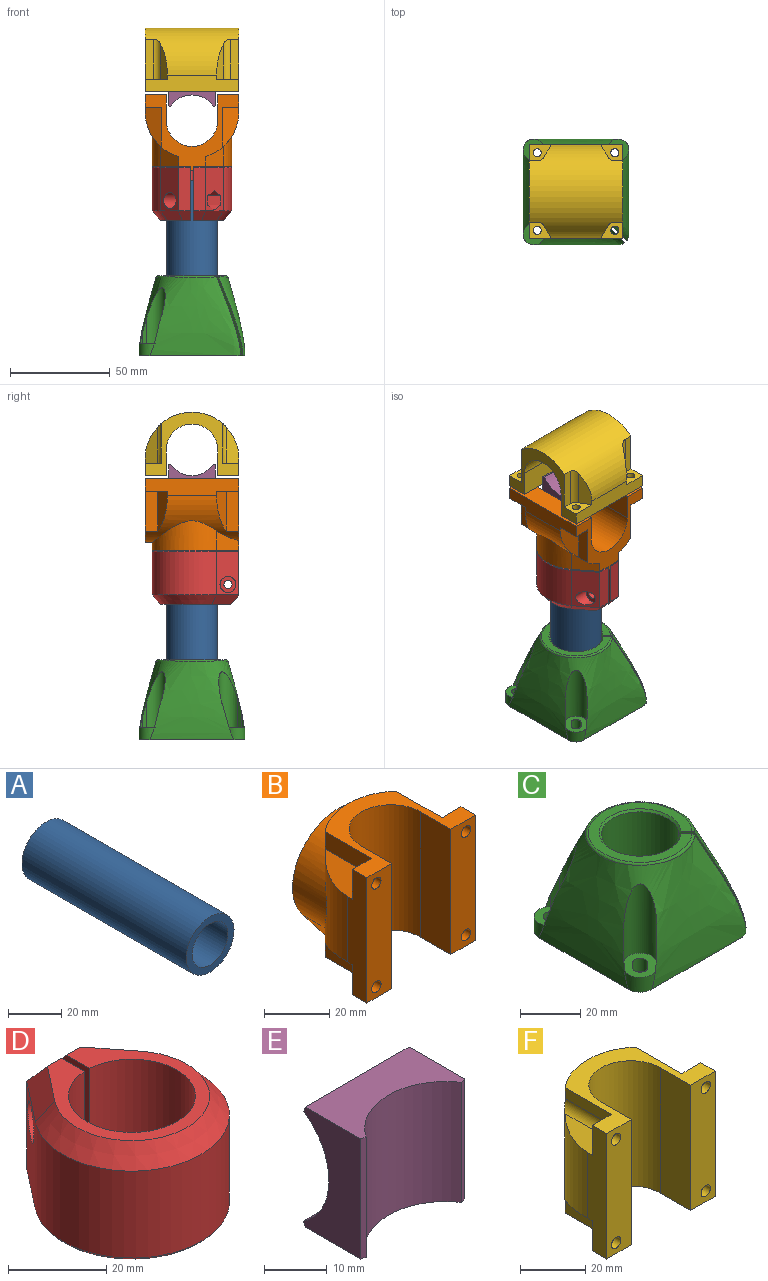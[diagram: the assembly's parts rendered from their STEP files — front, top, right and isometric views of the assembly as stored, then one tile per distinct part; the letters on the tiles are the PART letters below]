
ASSEMBLY  parts=6 mates=5
PART A: 4 faces, bbox 25.4x87x25.4 mm
  f0: cylinder r=9.5mm len=87mm, axis (0,-1,0), area 5193.1mm2, adj f2,f3
  f1: cylinder r=12.7mm len=87mm, axis (0,-1,0), area 6942.3mm2, adj f2,f3
  f2: plane 25.4x25.4mm, normal (0,1,0), area 223.2mm2, adj f0,f1
  f3: plane 25.4x25.4mm, normal (0,-1,0), area 223.2mm2, adj f0,f1
PART B: 35 faces, bbox 47x37.9x47 mm
  f0: plane 47x8.4mm, normal (1,0,0), area 346.6mm2, adj f2,f10,f11,f18,f30,f31,f32,f34
  f1: plane 47x8.4mm, normal (-1,0,0), area 346.6mm2, adj f2,f4,f10,f18,f23,f25,f27,f28
  f2: cylinder r=23.5mm len=47mm, axis (0,0,-1), area 1212.5mm2, adj f0,f1,f5,f6,f7,f10,f18,f23
  f3: cylinder r=12.85mm len=47mm, axis (0,0,-1), area 1889.1mm2, adj f8,f10,f16,f17,f18
  f4: plane 47x10.65mm, normal (0,-1,0), area 474.8mm2, adj f1,f10,f16,f18,f21,f22
  f5: plane 11.3x9.92mm, normal (0.79,0,-0.62), area 100.9mm2, adj f2,f6,f9,f10
  f6: cylinder r=19.8mm len=39.6mm, axis (0,1,0), area 902.1mm2, adj f2,f5,f7,f9
  f7: plane 11.3x9.92mm, normal (-0.79,0,-0.62), area 100.9mm2, adj f2,f6,f9,f10
  f8: cylinder r=2.02mm len=10.16mm, axis (0,1,0), area 128.3mm2, adj f3,f9
  f9: plane 43.3x39.6mm, normal (0,1,0), area 1288.9mm2, adj f5,f6,f7,f8,f10,f12,f13,f14
  f10: plane 47x37.9mm, normal (0,0,-1), area 490.6mm2, adj f0,f1,f2,f3,f4,f5,f7,f9
  f11: plane 47x10.65mm, normal (0,-1,0), area 474.8mm2, adj f0,f10,f17,f18,f19,f20
  f12: plane 10.8x2mm, normal (1,0,0), area 21.6mm2, adj f9,f10,f13,f15
  f13: cylinder r=0.75mm len=2mm, axis (0,-1,0), area 4.7mm2, adj f9,f12,f14,f15
  f14: plane 10.8x2mm, normal (-1,0,0), area 21.6mm2, adj f9,f10,f13,f15
  f15: plane 11.55x1.5mm, normal (0,1,0), area 17.1mm2, adj f10,f12,f13,f14
  f16: plane 47x13mm, normal (1,0,0), area 611mm2, adj f3,f4,f10,f18
  f17: plane 47x13mm, normal (-1,0,0), area 611mm2, adj f3,f10,f11,f18
  f18: plane 47x31.9mm, normal (0,0,1), area 429.2mm2, adj f0,f1,f2,f3,f4,f11,f16,f17
  f19: cylinder r=2.02mm len=6.25mm, axis (0,1,0), area 79.5mm2, adj f11,f34
  f20: cylinder r=2.02mm len=6.25mm, axis (0,1,0), area 79.5mm2, adj f11,f31
  f21: cylinder r=2.02mm len=6.25mm, axis (0,1,0), area 79.5mm2, adj f4,f28
  f22: cylinder r=2.02mm len=6.25mm, axis (0,1,0), area 79.5mm2, adj f4,f25
  f23: plane 19.99x8.2mm, normal (-0.5,0,0.87), area 137.6mm2, adj f1,f2,f24,f25
  f24: plane 19.99x6.47mm, normal (-1,0,0), area 129.3mm2, adj f2,f18,f23,f25
  f25: plane 11.2x8.2mm, normal (0,1,0), area 59.6mm2, adj f1,f18,f22,f23,f24
  f26: plane 19.99x6.47mm, normal (-1,0,0), area 129.3mm2, adj f2,f10,f27,f28
  f27: plane 19.99x8.2mm, normal (-0.5,0,-0.87), area 137.6mm2, adj f1,f2,f26,f28
  f28: plane 11.2x8.2mm, normal (0,1,0), area 59.6mm2, adj f1,f10,f21,f26,f27
  f29: plane 19.99x6.47mm, normal (1,0,0), area 129.3mm2, adj f2,f10,f30,f31
  f30: plane 19.99x8.2mm, normal (0.5,0,-0.87), area 137.6mm2, adj f0,f2,f29,f31
  f31: plane 11.2x8.2mm, normal (0,1,0), area 59.6mm2, adj f0,f10,f20,f29,f30
  f32: plane 19.99x8.2mm, normal (0.5,0,0.87), area 137.6mm2, adj f0,f2,f33,f34
  f33: plane 19.99x6.47mm, normal (1,0,0), area 129.3mm2, adj f2,f18,f32,f34
  f34: plane 11.2x8.2mm, normal (0,1,0), area 59.6mm2, adj f0,f18,f19,f32,f33
PART C: 56 faces, bbox 53.3x53.3x40.3 mm
  f0: bspline ~53x53mm, area 5579.9mm2, adj f13,f16,f17,f18,f19,f20,f21,f22
  f1: plane 5.25x2.12mm, normal (0.71,-0.71,0), area 15.7mm2, adj f2,f4,f35,f49
  f2: cylinder r=2.5mm len=5.25mm, axis (0,0,1), area 41.2mm2, adj f1,f3,f35,f50
  f3: plane 5.25x2.12mm, normal (-0.71,0.71,0), area 15.7mm2, adj f2,f4,f35,f48
  f4: cylinder r=2.5mm len=5.25mm, axis (0,0,1), area 41.2mm2, adj f1,f3,f35,f47
  f5: plane 5.25x2.12mm, normal (-0.71,-0.71,0), area 15.7mm2, adj f6,f8,f29,f45
  f6: cylinder r=2.5mm len=5.25mm, axis (0,0,1), area 41.2mm2, adj f5,f7,f29,f46
  f7: plane 5.25x2.12mm, normal (0.71,0.71,0), area 15.7mm2, adj f6,f8,f29,f44
  f8: cylinder r=2.5mm len=5.25mm, axis (0,0,1), area 41.2mm2, adj f5,f7,f29,f43
  f9: plane 5.25x2.12mm, normal (-0.71,0.71,0), area 15.7mm2, adj f10,f12,f23,f41
  f10: cylinder r=2.5mm len=5.25mm, axis (0,0,1), area 41.2mm2, adj f9,f11,f23,f42
  f11: plane 5.25x2.12mm, normal (0.71,-0.71,0), area 15.7mm2, adj f10,f12,f23,f40
  f12: cylinder r=2.5mm len=5.25mm, axis (0,0,1), area 41.2mm2, adj f9,f11,f23,f39
  f13: plane 53.28x53.28mm, normal (0,0,-1), area 1979.2mm2, adj f0,f36,f37,f38,f39,f40,f41,f42
  f14: plane 34.21x34.2mm, normal (0,0,1), area 340.7mm2, adj f16,f17,f51,f55
  f15: cylinder r=12.85mm len=38.5mm, axis (0,0,1), area 3050.7mm2, adj f16,f17,f51,f53
  f16: plane 39.27x15.79mm, normal (0.71,0.71,0), area 590.7mm2, adj f0,f14,f15,f51,f52,f55
  f17: plane 39.26x15.79mm, normal (-0.71,-0.71,0), area 592.4mm2, adj f0,f14,f15,f51,f54,f55
  f18: cylinder r=5.5mm len=5.12mm, axis (0,0,-1), area 4.7mm2, adj f0,f22,f23
  f19: cylinder r=5.5mm len=7.16mm, axis (0,0,-1), area 7.8mm2, adj f0,f20,f23
  f20: plane 15.57x2.42mm, normal (0.71,-0.71,0), area 34.5mm2, adj f0,f19,f21,f23
  f21: cylinder r=5.5mm len=28.05mm, axis (0,0,-1), area 394.3mm2, adj f0,f20,f22,f23
  f22: plane 12.96x2.34mm, normal (-0.71,0.71,0), area 27.2mm2, adj f0,f18,f21,f23
  f23: plane 13.12x13.12mm, normal (0,0,1), area 93.4mm2, adj f9,f10,f11,f12,f18,f19,f20,f21
  f24: cylinder r=5.5mm len=5.12mm, axis (0,0,-1), area 4.7mm2, adj f0,f28,f29
  f25: cylinder r=5.5mm len=7.16mm, axis (0,0,-1), area 7.8mm2, adj f0,f26,f29
  f26: plane 15.57x2.42mm, normal (0.71,0.71,0), area 34.5mm2, adj f0,f25,f27,f29
  f27: cylinder r=5.5mm len=28.05mm, axis (0,0,-1), area 394.3mm2, adj f0,f26,f28,f29
  f28: plane 12.96x2.34mm, normal (-0.71,-0.71,0), area 27.2mm2, adj f0,f24,f27,f29
  f29: plane 13.12x13.12mm, normal (0,0,1), area 93.4mm2, adj f5,f6,f7,f8,f24,f25,f26,f27
  f30: cylinder r=5.5mm len=5.12mm, axis (0,0,-1), area 4.7mm2, adj f0,f34,f35
  f31: cylinder r=5.5mm len=7.16mm, axis (0,0,-1), area 7.8mm2, adj f0,f32,f35
  f32: plane 15.57x2.42mm, normal (-0.71,0.71,0), area 34.5mm2, adj f0,f31,f33,f35
  f33: cylinder r=5.5mm len=28.05mm, axis (0,0,-1), area 394.3mm2, adj f0,f32,f34,f35
  f34: plane 12.96x2.34mm, normal (0.71,-0.71,0), area 27.2mm2, adj f0,f30,f33,f35
  f35: plane 13.12x13.12mm, normal (0,0,1), area 93.4mm2, adj f1,f2,f3,f4,f30,f31,f32,f33
  f36: cylinder r=5.5mm len=7.91mm, axis (0,0,-1), area 65.9mm2, adj f0,f13,f35
  f37: cylinder r=5.5mm len=7.91mm, axis (0,0,-1), area 65.9mm2, adj f0,f13,f29
  f38: cylinder r=5.5mm len=7.91mm, axis (0,0,-1), area 66mm2, adj f0,f13,f23
  f39: cone r=2.5mm half-angle=45deg, axis (0,0,-1), area 9.6mm2, adj f12,f13,f40,f41
  f40: plane 2.65x2.65mm, normal (0.5,-0.5,-0.71), area 3.2mm2, adj f11,f13,f39,f42
  f41: plane 2.65x2.65mm, normal (-0.5,0.5,-0.71), area 3.2mm2, adj f9,f13,f39,f42
  f42: cone r=2.5mm half-angle=45deg, axis (0,0,-1), area 9.6mm2, adj f10,f13,f40,f41
  f43: cone r=2.5mm half-angle=45deg, axis (0,0,-1), area 9.6mm2, adj f8,f13,f44,f45
  f44: plane 2.65x2.65mm, normal (0.5,0.5,-0.71), area 3.2mm2, adj f7,f13,f43,f46
  f45: plane 2.65x2.65mm, normal (-0.5,-0.5,-0.71), area 3.2mm2, adj f5,f13,f43,f46
  f46: cone r=2.5mm half-angle=45deg, axis (0,0,-1), area 9.6mm2, adj f6,f13,f44,f45
  f47: cone r=2.5mm half-angle=45deg, axis (0,0,-1), area 9.6mm2, adj f4,f13,f48,f49
  f48: plane 2.65x2.65mm, normal (-0.5,0.5,-0.71), area 3.2mm2, adj f3,f13,f47,f50
  f49: plane 2.65x2.65mm, normal (0.5,-0.5,-0.71), area 3.2mm2, adj f1,f13,f47,f50
  f50: cone r=2.5mm half-angle=45deg, axis (0,0,-1), area 9.6mm2, adj f2,f13,f48,f49
  f51: cone r=12.85mm half-angle=45deg, axis (0,0,1), area 86.5mm2, adj f14,f15,f16,f17
  f52: plane 16.22x15.83mm, normal (0.5,0.5,-0.71), area 23.2mm2, adj f0,f13,f16,f53
  f53: cone r=13.6mm half-angle=45deg, axis (0,0,-1), area 85.8mm2, adj f13,f15,f52,f54
  f54: plane 16.22x15.83mm, normal (-0.5,-0.5,-0.71), area 23.2mm2, adj f0,f13,f17,f53
  f55: bspline ~36.12x36.09mm, area 129.4mm2, adj f0,f14,f16,f17
PART D: 37 faces, bbox 40.9x44.6x28.3 mm
  f0: cylinder r=2.02mm len=6.25mm, axis (1,0,0), area 79.5mm2, adj f3,f36
  f1: cylinder r=0.75mm len=6.4mm, axis (0,0,-1), area 15.1mm2, adj f3,f4,f17,f26
  f2: cylinder r=2.02mm len=7mm, axis (0,0,-1), area 89.1mm2, adj f11,f26
  f3: plane 26.4x10.62mm, normal (-1,0,0), area 258mm2, adj f0,f1,f9,f10,f15,f20,f25
  f4: plane 26.4x10.62mm, normal (1,0,0), area 258mm2, adj f1,f5,f10,f19,f22,f25,f27
  f5: plane 21.64x6mm, normal (0,1,0), area 129.8mm2, adj f4,f6,f18,f22
  f6: plane 22.95x12.61mm, normal (-0.79,0.62,0), area 246.5mm2, adj f5,f7,f16,f24,f28
  f7: cylinder r=19.8mm len=39.6mm, axis (0,0,-1), area 1914.9mm2, adj f6,f8,f14,f23
  f8: plane 21.64x11.3mm, normal (0.79,0.62,0), area 236.4mm2, adj f7,f9,f12,f21,f30,f31,f32,f33
  f9: plane 21.64x6mm, normal (0,1,0), area 129.8mm2, adj f3,f8,f13,f20
  f10: plane 35.3x31.6mm, normal (0,0,1), area 314.7mm2, adj f3,f4,f20,f21,f22,f23,f24,f25
  f11: plane 42.3x38.6mm, normal (0,0,-1), area 1213.6mm2, adj f2,f12,f13,f14,f15,f16,f17,f18
  f12: plane 11.6x9.09mm, normal (0.6,0.47,-0.64), area 11.1mm2, adj f8,f11,f13,f14
  f13: plane 6x0.6mm, normal (0,0.77,-0.64), area 4.4mm2, adj f9,f11,f12,f15
  f14: cone r=19.8mm half-angle=40deg, axis (0,0,1), area 68mm2, adj f7,f11,f12,f16
  f15: plane 10.62x0.6mm, normal (-0.77,0,-0.64), area 8.1mm2, adj f3,f11,f13,f17
  f16: plane 11.6x9.09mm, normal (-0.6,0.47,-0.64), area 11.1mm2, adj f6,f11,f14,f18
  f17: cone r=1.25mm half-angle=40deg, axis (0,0,-1), area 2.4mm2, adj f1,f11,f15,f19
  f18: plane 6x0.6mm, normal (0,0.77,-0.64), area 4.4mm2, adj f5,f11,f16,f19
  f19: plane 10.62x0.6mm, normal (0.77,0,-0.64), area 8.1mm2, adj f4,f11,f17,f18
  f20: plane 6x4.77mm, normal (0,0.77,0.64), area 31.3mm2, adj f3,f9,f10,f21
  f21: plane 13.76x10.79mm, normal (0.6,0.47,0.64), area 83.2mm2, adj f8,f10,f20,f23
  f22: plane 6x4.77mm, normal (0,0.77,0.64), area 31.3mm2, adj f4,f5,f10,f24
  f23: cone r=15.8mm half-angle=40deg, axis (0,0,-1), area 495.1mm2, adj f7,f10,f21,f24
  f24: plane 13.76x10.79mm, normal (-0.6,0.47,0.64), area 83.2mm2, adj f6,f10,f22,f23
  f25: cylinder r=12.9mm len=25.8mm, axis (0,0,1), area 1591mm2, adj f3,f4,f10,f26
  f26: plane 25.8x25.78mm, normal (0,0,1), area 509mm2, adj f1,f2,f25
  f27: cylinder r=2.02mm len=6.25mm, axis (1,0,0), area 79.5mm2, adj f4,f29
  f28: cylinder r=4mm len=8mm, axis (1,0,0), area 104.6mm2, adj f6,f29
  f29: plane 8x8mm, normal (-1,0,0), area 37.4mm2, adj f27,f28
  f30: plane 4.73x0.85mm, normal (0,-1,0), area 4mm2, adj f8,f31,f35,f36
  f31: plane 4.1x4.06mm, normal (0,-0.5,-0.87), area 11.6mm2, adj f8,f30,f32,f36
  f32: plane 7.26x4.1mm, normal (0,0.5,-0.87), area 26.8mm2, adj f8,f31,f33,f36
  f33: plane 7.26x4.73mm, normal (0,1,0), area 34.4mm2, adj f8,f32,f34,f36
  f34: plane 7.26x4.1mm, normal (0,0.5,0.87), area 26.8mm2, adj f8,f33,f35,f36
  f35: plane 4.1x4.06mm, normal (0,-0.5,0.87), area 11.6mm2, adj f8,f30,f34,f36
  f36: plane 9.47x8.2mm, normal (1,0,0), area 45.3mm2, adj f0,f30,f31,f32,f33,f34,f35
PART E: 10 faces, bbox 23.4x13.1x23.4 mm
  f0: plane 23.4x12.75mm, normal (0,0,1), area 212.7mm2, adj f3,f4,f5,f6,f7,f9
  f1: plane 23.4x12.75mm, normal (0,0,-1), area 212.7mm2, adj f3,f4,f5,f6,f7,f8
  f2: cylinder r=12.9mm len=23.4mm, axis (-1,0,0), area 589.7mm2, adj f3,f4,f8,f9
  f3: plane 23.4x12.75mm, normal (1,0,0), area 212.7mm2, adj f0,f1,f2,f7,f8,f9
  f4: plane 23.4x12.75mm, normal (-1,0,0), area 212.7mm2, adj f0,f1,f2,f6,f8,f9
  f5: cylinder r=12.9mm len=23.4mm, axis (0,0,1), area 589.7mm2, adj f0,f1,f6,f7
  f6: plane 23.4x1.01mm, normal (-0.29,-0.96,0), area 24.7mm2, adj f0,f1,f4,f5
  f7: plane 23.4x1.01mm, normal (0.29,-0.96,0), area 24.7mm2, adj f0,f1,f3,f5
  f8: plane 23.4x1.01mm, normal (0,0.96,-0.29), area 24.7mm2, adj f1,f2,f3,f4
  f9: plane 23.4x1.01mm, normal (0,0.96,0.29), area 24.7mm2, adj f0,f2,f3,f4
PART F: 30 faces, bbox 47x31.9x47 mm
  f0: plane 47x8.4mm, normal (1,0,0), area 346.6mm2, adj f1,f2,f3,f7,f15,f17,f18,f21
  f1: cylinder r=23.5mm len=47mm, axis (0,0,-1), area 2698.4mm2, adj f0,f2,f3,f8,f14,f15,f16,f18
  f2: plane 47x31.9mm, normal (0,0,1), area 429.2mm2, adj f0,f1,f4,f5,f6,f7,f8,f9
  f3: plane 47x31.9mm, normal (0,0,-1), area 429.2mm2, adj f0,f1,f4,f5,f6,f7,f8,f9
  f4: plane 47x13mm, normal (1,0,0), area 611mm2, adj f2,f3,f5,f9
  f5: cylinder r=12.85mm len=47mm, axis (0,0,-1), area 1902.1mm2, adj f2,f3,f4,f6
  f6: plane 47x13mm, normal (-1,0,0), area 611mm2, adj f2,f3,f5,f7
  f7: plane 47x10.65mm, normal (0,-1,0), area 474.8mm2, adj f0,f2,f3,f6,f12,f13
  f8: plane 47x8.4mm, normal (-1,0,0), area 346.6mm2, adj f1,f2,f3,f9,f23,f25,f26,f29
  f9: plane 47x10.65mm, normal (0,-1,0), area 474.8mm2, adj f2,f3,f4,f8,f10,f11
  f10: cylinder r=2.02mm len=6.25mm, axis (0,-1,0), area 79.5mm2, adj f9,f29
  f11: cylinder r=2.02mm len=6.25mm, axis (0,-1,0), area 79.5mm2, adj f9,f25
  f12: cylinder r=2.02mm len=6.25mm, axis (0,-1,0), area 79.5mm2, adj f7,f21
  f13: cylinder r=2.02mm len=6.25mm, axis (0,-1,0), area 79.5mm2, adj f7,f17
  f14: cylinder r=4.1mm len=19.99mm, axis (0,-1,0), area 83mm2, adj f1,f15,f16,f17
  f15: plane 18x6.15mm, normal (0.5,0,0.87), area 92.5mm2, adj f0,f1,f14,f17
  f16: plane 19.99x4.1mm, normal (1,0,0), area 81.9mm2, adj f1,f2,f14,f17
  f17: plane 11.2x8.2mm, normal (0,1,0), area 58.7mm2, adj f0,f2,f13,f14,f15,f16
  f18: plane 18x6.15mm, normal (0.5,0,-0.87), area 92.5mm2, adj f0,f1,f19,f21
  f19: cylinder r=4.1mm len=19.99mm, axis (0,-1,0), area 83mm2, adj f1,f18,f20,f21
  f20: plane 19.99x4.1mm, normal (1,0,0), area 81.9mm2, adj f1,f3,f19,f21
  f21: plane 11.2x8.2mm, normal (0,1,0), area 58.7mm2, adj f0,f3,f12,f18,f19,f20
  f22: cylinder r=4.1mm len=19.99mm, axis (0,-1,0), area 83mm2, adj f1,f23,f24,f25
  f23: plane 18x6.15mm, normal (-0.5,0,-0.87), area 92.5mm2, adj f1,f8,f22,f25
  f24: plane 19.99x4.1mm, normal (-1,0,0), area 81.9mm2, adj f1,f3,f22,f25
  f25: plane 11.2x8.2mm, normal (0,1,0), area 58.7mm2, adj f3,f8,f11,f22,f23,f24
  f26: plane 18x6.15mm, normal (-0.5,0,0.87), area 92.5mm2, adj f1,f8,f27,f29
  f27: cylinder r=4.1mm len=19.99mm, axis (0,-1,0), area 83mm2, adj f1,f26,f28,f29
  f28: plane 19.99x4.1mm, normal (-1,0,0), area 81.9mm2, adj f1,f2,f27,f29
  f29: plane 11.2x8.2mm, normal (0,1,0), area 58.7mm2, adj f2,f8,f10,f26,f27,f28
PLACE A rot(axis=(1,0,0),90deg) t=(0.03,-0.03,0.75)mm
PLACE B rot(axis=(-1,0,0),90deg) t=(-93.12,-0.03,94.75)mm
PLACE C t=(0.03,-0.03,0)mm
PLACE D rot(axis=(1,0,0),180deg) t=(0.03,-0.03,81.25)mm
PLACE E rot(axis=(1,0,0),90deg) t=(0.03,-0.03,131.35)mm
PLACE F rot(axis=(0.58,-0.58,-0.58),120deg) t=(0.03,-0.03,140.45)mm
MATE fastened D.f25 <-> A.f1  axis (0,0,-1) through (0.03,-0.03,87.75)mm
MATE fastened A.f1 <-> C.f15  axis (0,0,-1) through (0.03,-0.03,0.75)mm
MATE fastened B.f8 <-> D.f2  axis (0,0,-1) through (0.03,-0.03,94.75)mm
MATE fastened F.f5 <-> E.f2  axis (1,0,0) through (0.03,-0.03,145.1)mm
MATE fastened E.f5 <-> B.f3  axis (0,-1,0) through (0.03,-0.03,117.6)mm
